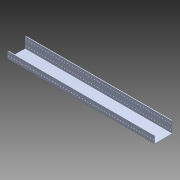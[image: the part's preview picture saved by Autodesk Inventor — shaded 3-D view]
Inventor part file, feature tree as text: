
AUTODESK INVENTOR PART (.ipt)
format: ipt  version: 2015 (Build 190159000, 159)  size: 426,496 bytes
history: native  units: in
note: dims shown in document units (in); Inventor stores cm internally (conversion verified against a paired STEP export)
features: projected_geometry x7, other x2, extrude x1, chamfer x1, imported_body x1, sketch x1
ambient origin geometry x8: Origin, YZ Plane, XZ Plane, XY Plane, X Axis, Y Axis, Z Axis, Center Point
bodies: Body1 (feature_tree)
feature tree (13):
  other  "LPattern4"
  other  "AM14U2 End Sheet1"
  extrude  "Extrusion1"  Depth=0.125in TaperAngle=45.0deg
  chamfer  "Chamfer1"  [1 undecoded]
  imported_body  "Base1"
  sketch  "Sketch1"  dims[d0=4.0in d1=0.0in d2=0.125in d3=0.125in d4=45.0deg]
  projected_geometry  "Projected Loop1"
  projected_geometry  "Projected Loop2"
  projected_geometry  "Projected Loop3"
  projected_geometry  "Projected Loop4"
  projected_geometry  "Projected Loop5"
  projected_geometry  "Projected Loop6"
  projected_geometry  "Projected Loop7"
note: 1 required parameter value undecoded (feature->parameter linkage not recoverable at this tier; creation-order binding heuristic only, values carry confidence <= 0.55)
